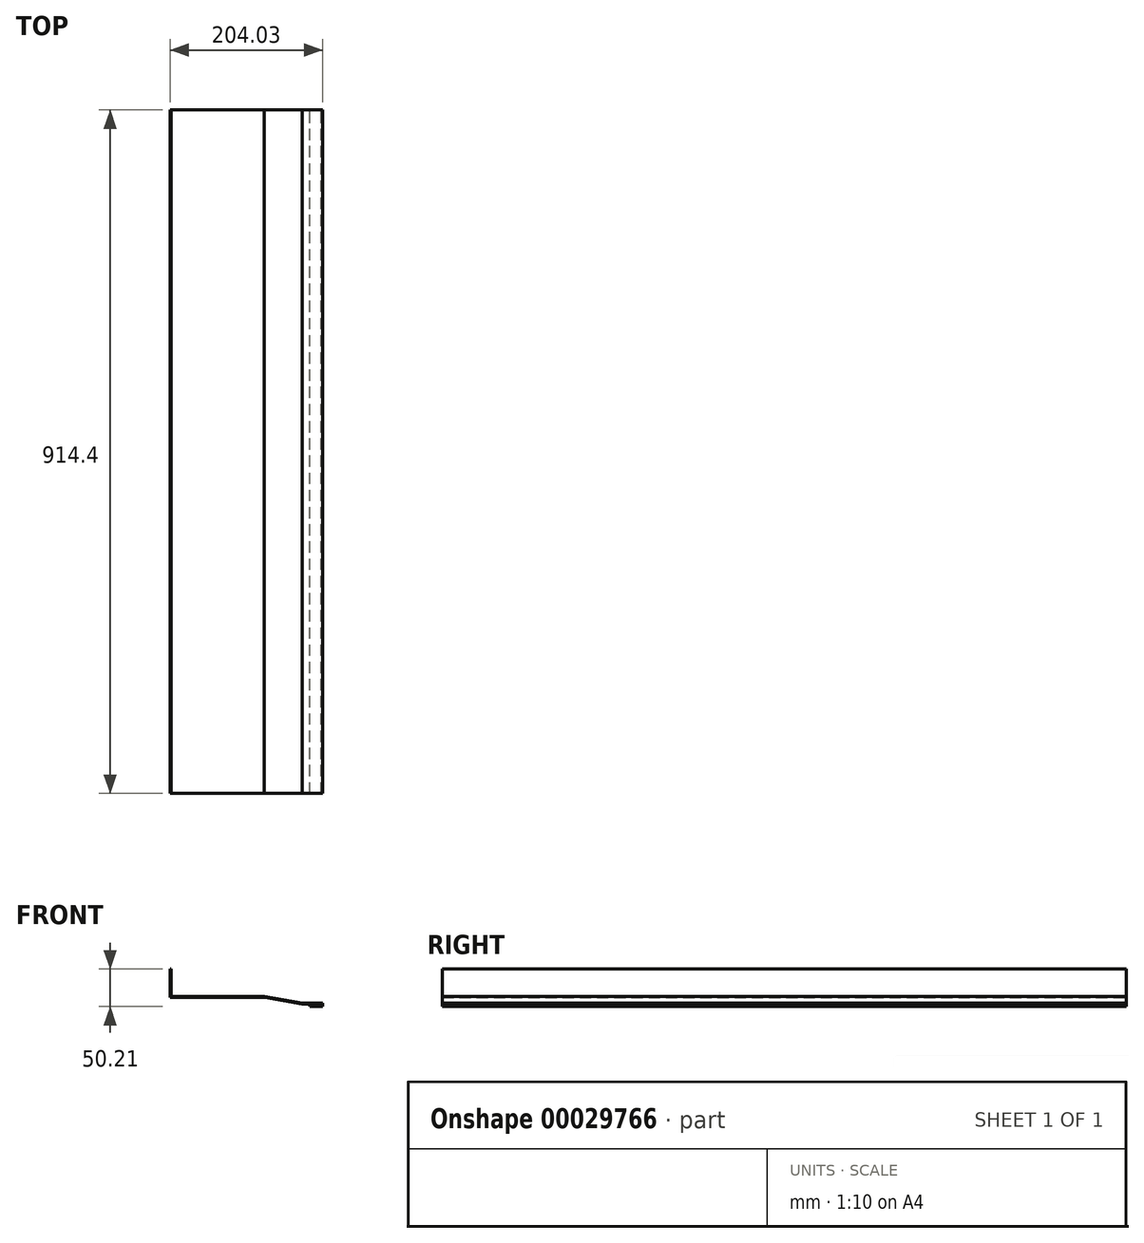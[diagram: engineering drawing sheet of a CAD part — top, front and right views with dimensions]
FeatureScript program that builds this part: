
annotation { "Feature Type Name" : "Feature", "Feature Type Description" : "" }
export const myFeature = defineFeature(function(context is Context, id is Id, definition is map)
    precondition{}
    {
        {
            var Q0;
            Q0=qCreatedBy(makeId("Front.planeOp"),FACE);
            var sketch = newSketch(context, id + "F0", { "sketchPlane" : qUnion([Q0])});
            skLineSegment(sketch, "E0", {"start": v(-123.98, -1.61) * mm, "end": v(3.02, -1.61) * mm});
            skLineSegment(sketch, "E1", {"start": v(3.02, -1.61) * mm, "end": v(53.04, -10.5) * mm});
            skLineSegment(sketch, "E2", {"start": v(53.04, -10.5) * mm, "end": v(78.44, -10.5) * mm});
            skLineSegment(sketch, "E3", {"start": v(78.44, -10.5) * mm, "end": v(78.44, -12.1) * mm});
            skLineSegment(sketch, "E4", {"start": v(78.44, -12.1) * mm, "end": v(62.74, -12.1) * mm});
            skLineSegment(sketch, "E5", {"start": v(62.74, -12.1) * mm, "end": v(62.74, -13.72) * mm});
            skLineSegment(sketch, "E6", {"start": v(62.74, -13.72) * mm, "end": v(80.05, -13.72) * mm});
            skLineSegment(sketch, "E7", {"start": v(80.05, -13.72) * mm, "end": v(80.05, -8.88) * mm});
            skLineSegment(sketch, "E8", {"start": v(80.05, -8.88) * mm, "end": v(52.54, -8.88) * mm});
            skLineSegment(sketch, "E9", {"start": v(52.54, -8.88) * mm, "end": v(2.2, 0) * mm});
            skLineSegment(sketch, "E10", {"start": v(2.2, 0) * mm, "end": v(-122.37, 0) * mm});
            skLineSegment(sketch, "E11", {"start": v(-122.37, 0) * mm, "end": v(-122.37, 36.49) * mm});
            skLineSegment(sketch, "E12", {"start": v(-122.37, 36.49) * mm, "end": v(-123.98, 36.49) * mm});
            skLineSegment(sketch, "E13", {"start": v(-123.98, 36.49) * mm, "end": v(-123.98, -1.61) * mm});
            skSolve(sketch);
        }
        {
            var Q0;
            Q0=makeQuery(id+"F0.imprint","IMPRINT",FACE,{"disambiguationData":[TD([[makeQuery(id+"F0.imprint","IMPRINT",EDGE,{"derivedFrom":sQuery(id+"F0.wireOp",EDGE,"E0")}),1.0]])]});
            extrude(context, id + "F1", {"entities" : qUnion([Q0]), "depth" : 914.4 * mm});
        }
    });
